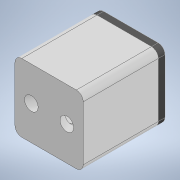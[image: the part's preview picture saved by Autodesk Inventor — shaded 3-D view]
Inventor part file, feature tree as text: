
AUTODESK INVENTOR PART (.ipt)
format: ipt  version: 2022 (Build 260153000, 153)  size: 19,067,392 bytes
history: native  units: mm
features: sketch x5, extrude x3, projected_geometry x3, other x1, move_body x1, revolve x1, sweep x1, pattern_circular x1, fillet x1, hole x1, chamfer x1
ambient origin geometry x8: Origin, YZ Plane, XZ Plane, XY Plane, X Axis, Y Axis, Z Axis, Center Point
bodies: Solid1 (feature_tree), Solid2 (feature_tree)
feature tree (19):
  other  "MeshFeature1"
  move_body  "Move Body1"
  sketch  "Sketch1"  dims[d0=-263.204mm d1=-210.1mm d2=-54.192mm d3=5.0mm]
  extrude  "Extrusion1"  Depth=5.0mm
  revolve  "Revolution1"  [1 undecoded]
  sweep  "Sweep1"
  extrude  "Extrusion2"  Depth=40.0mm TaperAngle=0.0deg
  pattern_circular  "Circular Pattern1"  [2 undecoded]
  fillet  "Fillet1"  [1 undecoded]
  hole  "Hole1"  [1 undecoded]
  extrude  "Extrusion3"  Depth=2.0mm TaperAngle=360.0deg
  chamfer  "Chamfer1"  Distance=4.0mm
  sketch  "Sketch2"  dims[d4=8.0mm d5=30.0mm]
  sketch  "Sketch3"  dims[d6=16.0mm d7=39.0mm]
  projected_geometry  "Projected Loop1"
  sketch  "Sketch4"  dims[d8=40.0mm d9=40.0mm d10=0.0mm]
  projected_geometry  "Projected Loop2"
  sketch  "Sketch5"  dims[d11=90.0deg d12=8.0mm d13=0.0mm d14=0.0mm d15=4.0mm d16=0.0mm d17=20.0mm d18=360.0deg d20=4.0mm d21=4.0mm d22=6.0mm d23=4.0mm d24=2.0mm d25=90.0deg d26=14.0mm d27=0.0mm d28=4.0mm d29=0.0mm d30=1.0mm d31=2.0mm d32=45.0deg]
  projected_geometry  "Projected Loop3"
note: 5 required parameter values undecoded (feature->parameter linkage not recoverable at this tier; creation-order binding heuristic only, values carry confidence <= 0.55)